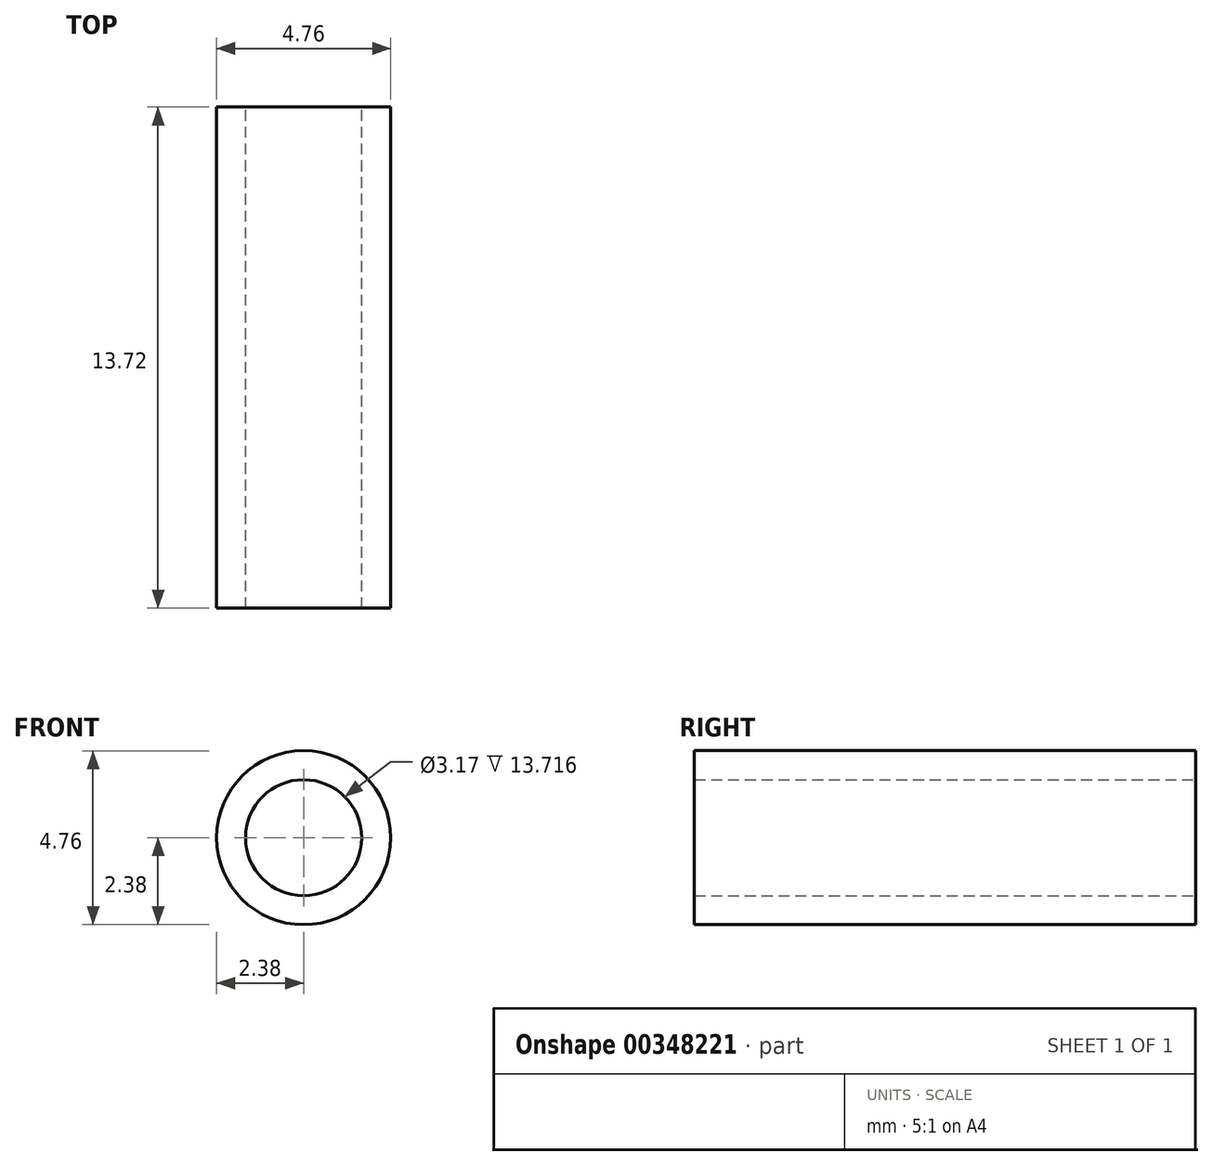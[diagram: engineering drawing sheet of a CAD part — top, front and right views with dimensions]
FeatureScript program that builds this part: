
annotation { "Feature Type Name" : "Feature", "Feature Type Description" : "" }
export const myFeature = defineFeature(function(context is Context, id is Id, definition is map)
    precondition{}
    {
        {
            var Q0;
            Q0=qCreatedBy(makeId("Front.planeOp"),FACE);
            var sketch = newSketch(context, id + "F0", { "sketchPlane" : qUnion([Q0])});
            skCircle(sketch, "E0", {"center": v(0, 0) * mm, "radius": 1.59 * mm});
            skCircle(sketch, "E1", {"center": v(0, 0) * mm, "radius": 2.38 * mm});
            skSolve(sketch);
        }
        {
            var Q0;
            Q0=qSketchRegion(id+"F0",true);
            extrude(context, id + "F1", {"entities" : qUnion([Q0]), "endBound" : BoundingType.SYMMETRIC, "depth" : 13.72 * mm});
        }
    });
